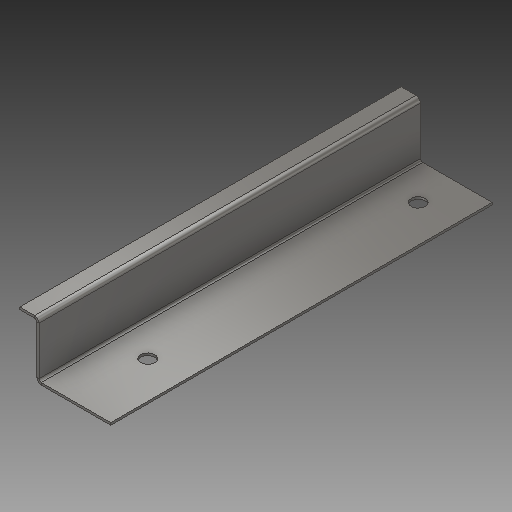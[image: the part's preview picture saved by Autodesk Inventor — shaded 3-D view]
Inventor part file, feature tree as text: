
AUTODESK INVENTOR PART (.ipt)
format: ipt  version: 2017 (Build 210142000, 142)  size: 151,040 bytes
history: native  units: in
note: dims shown in document units (in); Inventor stores cm internally (conversion verified against a paired STEP export)
features: other x3, sketch x2
ambient origin geometry x8: Origin, YZ Plane, XZ Plane, XY Plane, X Axis, Y Axis, Z Axis, Center Point
bodies: Solid1 (feature_tree)
feature tree (5):
  other  "Chapa Fixação Pé Nivelador.ipt"
  other  "Solid1::Chapa Fixação Pé Nivelador.ipt"
  other  "TaggingFeature1"
  sketch  "Sketch1"  dims[d0=0.3937in]
  sketch  "Sketch2"
